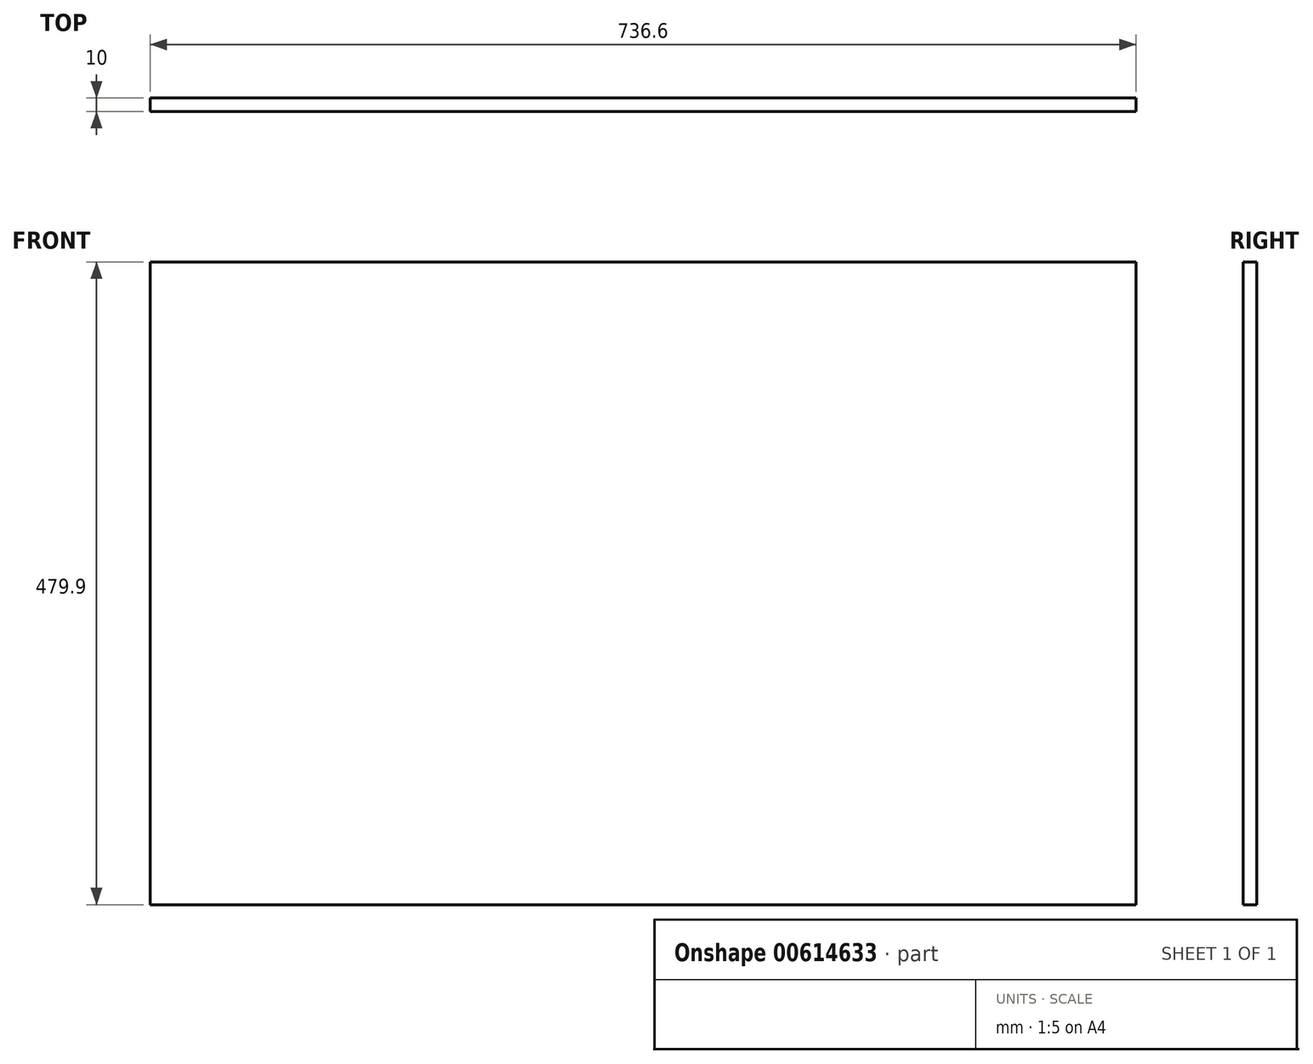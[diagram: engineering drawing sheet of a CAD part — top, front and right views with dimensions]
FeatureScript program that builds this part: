
annotation { "Feature Type Name" : "Feature", "Feature Type Description" : "" }
export const myFeature = defineFeature(function(context is Context, id is Id, definition is map)
    precondition{}
    {
        {
            var Q0;
            Q0=qCreatedBy(makeId("Front.planeOp"),FACE);
            var sketch = newSketch(context, id + "F0", { "sketchPlane" : qUnion([Q0])});
            skLineSegment(sketch, "E0.bottom", {"start": v(368.3, -239.95) * mm, "end": v(-368.3, -239.95) * mm});
            skLineSegment(sketch, "E0.top", {"start": v(368.3, 239.95) * mm, "end": v(-368.3, 239.95) * mm});
            skLineSegment(sketch, "E0.left", {"start": v(368.3, -239.95) * mm, "end": v(368.3, 239.95) * mm});
            skLineSegment(sketch, "E0.right", {"start": v(-368.3, -239.95) * mm, "end": v(-368.3, 239.95) * mm});
            skPoint(sketch, "E0.middle", {"position": v(0, 0) * mm});
            skSolve(sketch);
        }
        {
            var Q0;
            Q0=makeQuery(id+"F0.imprint","IMPRINT",FACE,{"disambiguationData":[TD([[makeQuery(id+"F0.imprint","IMPRINT",EDGE,{"derivedFrom":sQuery(id+"F0.wireOp",EDGE,"E0.bottom")}),-1.0]])]});
            extrude(context, id + "F1", {"entities" : qUnion([Q0]), "depth" : 10 * mm});
        }
    });
